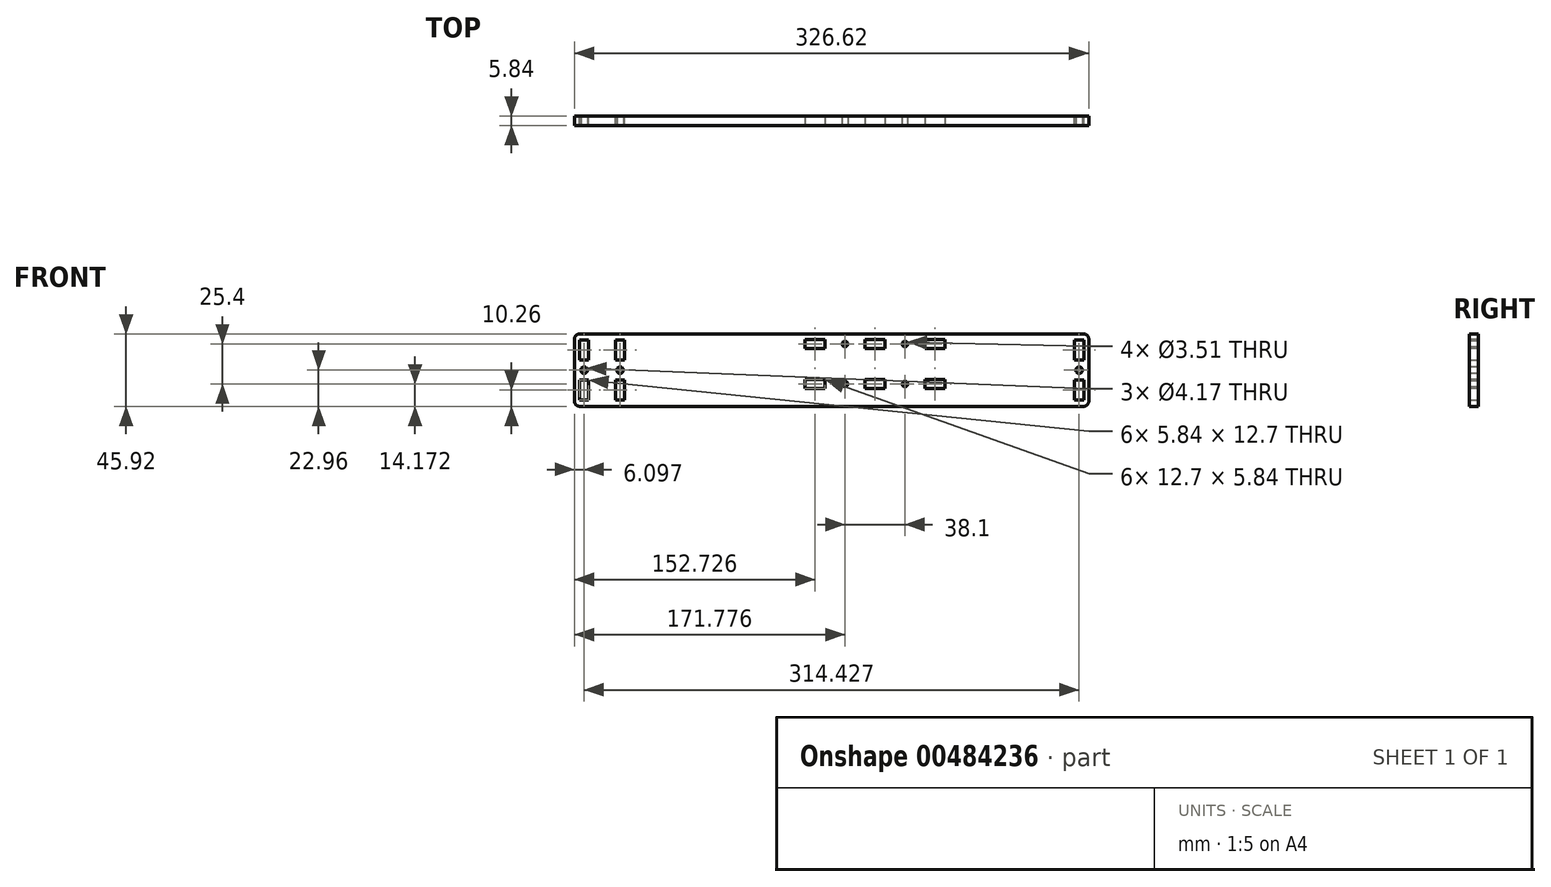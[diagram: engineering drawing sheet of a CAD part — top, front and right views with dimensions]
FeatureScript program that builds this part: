
annotation { "Feature Type Name" : "Feature", "Feature Type Description" : "" }
export const myFeature = defineFeature(function(context is Context, id is Id, definition is map)
    precondition{}
    {
        {
            var Q0;
            Q0=qCreatedBy(makeId("Front.planeOp"),FACE);
            var sketch = newSketch(context, id + "F0", { "sketchPlane" : qUnion([Q0])});
            skLineSegment(sketch, "E0.bottom", {"start": v(-163.3, 22.96) * mm, "end": v(163.3, 22.96) * mm});
            skLineSegment(sketch, "E0.top", {"start": v(-163.3, -22.96) * mm, "end": v(163.3, -22.96) * mm});
            skLineSegment(sketch, "E0.left", {"start": v(-163.3, 22.96) * mm, "end": v(-163.3, -22.96) * mm});
            skLineSegment(sketch, "E0.right", {"start": v(163.3, 22.96) * mm, "end": v(163.3, -22.96) * mm});
            skPoint(sketch, "E0.middle", {"position": v(0, 0) * mm});
            skLineSegment(sketch, "E1", {"start": v(-163.3, 0) * mm, "end": v(163.3, 0) * mm, "construction": true});
            skLineSegment(sketch, "E2.bottom", {"start": v(-160.13, 6.35) * mm, "end": v(-154.3, 6.35) * mm});
            skLineSegment(sketch, "E2.top", {"start": v(-160.13, 19.05) * mm, "end": v(-154.3, 19.05) * mm});
            skLineSegment(sketch, "E2.left", {"start": v(-160.13, 6.35) * mm, "end": v(-160.13, 19.05) * mm});
            skLineSegment(sketch, "E2.right", {"start": v(-154.3, 6.35) * mm, "end": v(-154.3, 19.05) * mm});
            skPoint(sketch, "E2.middle", {"position": v(-157.21, 12.7) * mm});
            skLineSegment(sketch, "E3.MirrorCS", {"start": v(-154.3, -6.35) * mm, "end": v(-154.3, -19.05) * mm});
            skLineSegment(sketch, "E4.MirrorCS", {"start": v(-160.13, -6.35) * mm, "end": v(-160.13, -19.05) * mm});
            skLineSegment(sketch, "E5.MirrorCS", {"start": v(-160.13, -19.05) * mm, "end": v(-154.3, -19.05) * mm});
            skLineSegment(sketch, "E6.MirrorCS", {"start": v(-160.13, -6.35) * mm, "end": v(-154.3, -6.35) * mm});
            skPoint(sketch, "E7.MirrorP", {"position": v(-157.21, -12.7) * mm});
            skLineSegment(sketch, "E8", {"start": v(-145.8, 22.96) * mm, "end": v(-145.8, -22.96) * mm, "construction": true});
            skPoint(sketch, "E9.MirrorP", {"position": v(-134.38, -12.7) * mm});
            skPoint(sketch, "E10.MirrorP", {"position": v(-134.38, 12.7) * mm});
            skLineSegment(sketch, "E11.MirrorCS", {"start": v(-131.46, -6.35) * mm, "end": v(-137.3, -6.35) * mm});
            skLineSegment(sketch, "E12.MirrorCS", {"start": v(-131.46, -19.05) * mm, "end": v(-137.3, -19.05) * mm});
            skLineSegment(sketch, "E13.MirrorCS", {"start": v(-131.46, -6.35) * mm, "end": v(-131.46, -19.05) * mm});
            skLineSegment(sketch, "E14.MirrorCS", {"start": v(-128.28, 0) * mm, "end": v(-454.9, 0) * mm, "construction": true});
            skLineSegment(sketch, "E15.MirrorCS", {"start": v(-137.3, -6.35) * mm, "end": v(-137.3, -19.05) * mm});
            skLineSegment(sketch, "E16.MirrorCS", {"start": v(-137.3, 6.35) * mm, "end": v(-137.3, 19.05) * mm});
            skLineSegment(sketch, "E17.MirrorCS", {"start": v(-131.46, 6.35) * mm, "end": v(-131.46, 19.05) * mm});
            skLineSegment(sketch, "E18.MirrorCS", {"start": v(-131.46, 19.05) * mm, "end": v(-137.3, 19.05) * mm});
            skLineSegment(sketch, "E19.MirrorCS", {"start": v(-131.46, 6.35) * mm, "end": v(-137.3, 6.35) * mm});
            skLineSegment(sketch, "E20", {"start": v(154.3, 22.96) * mm, "end": v(154.3, -22.96) * mm, "construction": true});
            skLineSegment(sketch, "E21.bottom", {"start": v(154.3, 19.05) * mm, "end": v(160.13, 19.05) * mm});
            skLineSegment(sketch, "E21.top", {"start": v(154.3, 6.35) * mm, "end": v(160.13, 6.35) * mm});
            skLineSegment(sketch, "E21.left", {"start": v(154.3, 19.05) * mm, "end": v(154.3, 6.35) * mm});
            skLineSegment(sketch, "E21.right", {"start": v(160.13, 19.05) * mm, "end": v(160.13, 6.35) * mm});
            skPoint(sketch, "E21.middle", {"position": v(157.21, 12.7) * mm});
            skLineSegment(sketch, "E22.MirrorCS", {"start": v(154.3, -19.05) * mm, "end": v(154.3, -6.35) * mm});
            skLineSegment(sketch, "E23.MirrorCS", {"start": v(154.3, -19.05) * mm, "end": v(160.13, -19.05) * mm});
            skPoint(sketch, "E24.MirrorP", {"position": v(157.21, -12.7) * mm});
            skLineSegment(sketch, "E25.MirrorCS", {"start": v(154.3, -6.35) * mm, "end": v(160.13, -6.35) * mm});
            skLineSegment(sketch, "E26.MirrorCS", {"start": v(160.13, -19.05) * mm, "end": v(160.13, -6.35) * mm});
            skSolve(sketch);
        }
        {
            var Q0;
            Q0 = qSketchRegion(id + "F0", true);
            extrude(context, id + "F1", {"entities" : qUnion([Q0]), "depth" : 5.84 * mm});
        }
        {
            var Q0;
            Q0=makeQuery(id+"F1.opExtrude","SWEPT_EDGE",EDGE,{"disambiguationData":[OSD([sQuery(id+"F0.wireOp",EDGE,"E0.bottom"),sQuery(id+"F0.wireOp",EDGE,"E0.left")])]});
            var Q1;
            Q1=makeQuery(id+"F1.opExtrude","SWEPT_EDGE",EDGE,{"disambiguationData":[OSD([sQuery(id+"F0.wireOp",EDGE,"E0.top"),sQuery(id+"F0.wireOp",EDGE,"E0.left")])]});
            var Q2;
            Q2=makeQuery(id+"F1.opExtrude","SWEPT_EDGE",EDGE,{"disambiguationData":[OSD([sQuery(id+"F0.wireOp",EDGE,"E0.bottom"),sQuery(id+"F0.wireOp",EDGE,"E0.right")])]});
            var Q3;
            Q3=makeQuery(id+"F1.opExtrude","SWEPT_EDGE",EDGE,{"disambiguationData":[OSD([sQuery(id+"F0.wireOp",EDGE,"E0.top"),sQuery(id+"F0.wireOp",EDGE,"E0.right")])]});
            fillet(context, id + "F2", {"entities" : qUnion([Q0, Q1, Q2, Q3]), "radius" : 3.17 * mm, "tangentPropagation" : true, "allowEdgeOverflow" : false});
        }
        {
            var Q0;
            Q0=makeQuery(id+"F1.opExtrude","CAP_FACE",FACE,{"disambiguationData":[OSD([sQuery(id+"F0.wireOp",EDGE,"E0.bottom"),sQuery(id+"F0.wireOp",EDGE,"E0.top"),sQuery(id+"F0.wireOp",EDGE,"E0.left"),sQuery(id+"F0.wireOp",EDGE,"E0.right"),sQuery(id+"F0.wireOp",EDGE,"E2.bottom"),sQuery(id+"F0.wireOp",EDGE,"E2.top"),sQuery(id+"F0.wireOp",EDGE,"E2.left"),sQuery(id+"F0.wireOp",EDGE,"E2.right"),sQuery(id+"F0.wireOp",EDGE,"E3.MirrorCS"),sQuery(id+"F0.wireOp",EDGE,"E4.MirrorCS"),sQuery(id+"F0.wireOp",EDGE,"E5.MirrorCS"),sQuery(id+"F0.wireOp",EDGE,"E6.MirrorCS"),sQuery(id+"F0.wireOp",EDGE,"E11.MirrorCS"),sQuery(id+"F0.wireOp",EDGE,"E12.MirrorCS"),sQuery(id+"F0.wireOp",EDGE,"E13.MirrorCS"),sQuery(id+"F0.wireOp",EDGE,"E15.MirrorCS"),sQuery(id+"F0.wireOp",EDGE,"E16.MirrorCS"),sQuery(id+"F0.wireOp",EDGE,"E17.MirrorCS"),sQuery(id+"F0.wireOp",EDGE,"E18.MirrorCS"),sQuery(id+"F0.wireOp",EDGE,"E19.MirrorCS"),sQuery(id+"F0.wireOp",EDGE,"E21.bottom"),sQuery(id+"F0.wireOp",EDGE,"E21.top"),sQuery(id+"F0.wireOp",EDGE,"E21.left"),sQuery(id+"F0.wireOp",EDGE,"E21.right"),sQuery(id+"F0.wireOp",EDGE,"E22.MirrorCS"),sQuery(id+"F0.wireOp",EDGE,"E23.MirrorCS"),sQuery(id+"F0.wireOp",EDGE,"E25.MirrorCS"),sQuery(id+"F0.wireOp",EDGE,"E26.MirrorCS")])],"isStart":false});
            var sketch = newSketch(context, id + "F3", { "sketchPlane" : qUnion([Q0])});
            skLineSegment(sketch, "E27", {"start": v(-157.21, 6.35) * mm, "end": v(-157.21, -6.35) * mm, "construction": true});
            skLineSegment(sketch, "E28", {"start": v(-134.38, -6.35) * mm, "end": v(-134.38, 6.35) * mm, "construction": true});
            skCircle(sketch, "E29", {"center": v(-134.38, 0) * mm, "radius": 2.08 * mm});
            skCircle(sketch, "E30", {"center": v(-157.21, 0) * mm, "radius": 2.08 * mm});
            skSolve(sketch);
        }
        {
            var Q0;
            Q0 = qSketchRegion(id + "F3", true);
            extrude(context, id + "F4", {"entities" : qUnion([Q0]), "operationType" : NewBodyOperationType.REMOVE, "oppositeDirection" : true, "depth" : 25.4 * mm});
        }
        {
            var Q0;
            Q0=makeQuery(id+"F1.opExtrude","CAP_FACE",FACE,{"disambiguationData":[OSD([sQuery(id+"F0.wireOp",EDGE,"E0.bottom"),sQuery(id+"F0.wireOp",EDGE,"E0.top"),sQuery(id+"F0.wireOp",EDGE,"E0.left"),sQuery(id+"F0.wireOp",EDGE,"E0.right"),sQuery(id+"F0.wireOp",EDGE,"E2.bottom"),sQuery(id+"F0.wireOp",EDGE,"E2.top"),sQuery(id+"F0.wireOp",EDGE,"E2.left"),sQuery(id+"F0.wireOp",EDGE,"E2.right"),sQuery(id+"F0.wireOp",EDGE,"E3.MirrorCS"),sQuery(id+"F0.wireOp",EDGE,"E4.MirrorCS"),sQuery(id+"F0.wireOp",EDGE,"E5.MirrorCS"),sQuery(id+"F0.wireOp",EDGE,"E6.MirrorCS"),sQuery(id+"F0.wireOp",EDGE,"E11.MirrorCS"),sQuery(id+"F0.wireOp",EDGE,"E12.MirrorCS"),sQuery(id+"F0.wireOp",EDGE,"E13.MirrorCS"),sQuery(id+"F0.wireOp",EDGE,"E15.MirrorCS"),sQuery(id+"F0.wireOp",EDGE,"E16.MirrorCS"),sQuery(id+"F0.wireOp",EDGE,"E17.MirrorCS"),sQuery(id+"F0.wireOp",EDGE,"E18.MirrorCS"),sQuery(id+"F0.wireOp",EDGE,"E19.MirrorCS"),sQuery(id+"F0.wireOp",EDGE,"E21.bottom"),sQuery(id+"F0.wireOp",EDGE,"E21.top"),sQuery(id+"F0.wireOp",EDGE,"E21.left"),sQuery(id+"F0.wireOp",EDGE,"E21.right"),sQuery(id+"F0.wireOp",EDGE,"E22.MirrorCS"),sQuery(id+"F0.wireOp",EDGE,"E23.MirrorCS"),sQuery(id+"F0.wireOp",EDGE,"E25.MirrorCS"),sQuery(id+"F0.wireOp",EDGE,"E26.MirrorCS")])],"isStart":false});
            var sketch = newSketch(context, id + "F5", { "sketchPlane" : qUnion([Q0])});
            skLineSegment(sketch, "E31", {"start": v(157.21, 6.35) * mm, "end": v(157.21, -6.35) * mm, "construction": true});
            skCircle(sketch, "E32", {"center": v(157.21, 0) * mm, "radius": 2.08 * mm});
            skSolve(sketch);
        }
        {
            var Q0;
            Q0 = qSketchRegion(id + "F5", true);
            extrude(context, id + "F6", {"entities" : qUnion([Q0]), "operationType" : NewBodyOperationType.REMOVE, "oppositeDirection" : true, "depth" : 25.4 * mm});
        }
        {
            var Q0;
            Q0=makeQuery(id+"F1.opExtrude","CAP_FACE",FACE,{"disambiguationData":[OSD([sQuery(id+"F0.wireOp",EDGE,"E0.bottom"),sQuery(id+"F0.wireOp",EDGE,"E0.top"),sQuery(id+"F0.wireOp",EDGE,"E0.left"),sQuery(id+"F0.wireOp",EDGE,"E0.right"),sQuery(id+"F0.wireOp",EDGE,"E2.bottom"),sQuery(id+"F0.wireOp",EDGE,"E2.top"),sQuery(id+"F0.wireOp",EDGE,"E2.left"),sQuery(id+"F0.wireOp",EDGE,"E2.right"),sQuery(id+"F0.wireOp",EDGE,"E3.MirrorCS"),sQuery(id+"F0.wireOp",EDGE,"E4.MirrorCS"),sQuery(id+"F0.wireOp",EDGE,"E5.MirrorCS"),sQuery(id+"F0.wireOp",EDGE,"E6.MirrorCS"),sQuery(id+"F0.wireOp",EDGE,"E11.MirrorCS"),sQuery(id+"F0.wireOp",EDGE,"E12.MirrorCS"),sQuery(id+"F0.wireOp",EDGE,"E13.MirrorCS"),sQuery(id+"F0.wireOp",EDGE,"E15.MirrorCS"),sQuery(id+"F0.wireOp",EDGE,"E16.MirrorCS"),sQuery(id+"F0.wireOp",EDGE,"E17.MirrorCS"),sQuery(id+"F0.wireOp",EDGE,"E18.MirrorCS"),sQuery(id+"F0.wireOp",EDGE,"E19.MirrorCS"),sQuery(id+"F0.wireOp",EDGE,"E21.bottom"),sQuery(id+"F0.wireOp",EDGE,"E21.top"),sQuery(id+"F0.wireOp",EDGE,"E21.left"),sQuery(id+"F0.wireOp",EDGE,"E21.right"),sQuery(id+"F0.wireOp",EDGE,"E22.MirrorCS"),sQuery(id+"F0.wireOp",EDGE,"E23.MirrorCS"),sQuery(id+"F0.wireOp",EDGE,"E25.MirrorCS"),sQuery(id+"F0.wireOp",EDGE,"E26.MirrorCS")])],"isStart":false});
            var sketch = newSketch(context, id + "F7", { "sketchPlane" : qUnion([Q0])});
            skLineSegment(sketch, "E33", {"start": v(-163.3, 16.61) * mm, "end": v(-4.23, 16.61) * mm, "construction": true});
            skLineSegment(sketch, "E34.bottom", {"start": v(-4.23, 19.53) * mm, "end": v(-16.93, 19.53) * mm});
            skLineSegment(sketch, "E34.top", {"start": v(-4.23, 13.7) * mm, "end": v(-16.93, 13.7) * mm});
            skLineSegment(sketch, "E34.left", {"start": v(-4.23, 19.53) * mm, "end": v(-4.23, 13.7) * mm});
            skLineSegment(sketch, "E34.right", {"start": v(-16.93, 19.53) * mm, "end": v(-16.93, 13.7) * mm});
            skPoint(sketch, "E34.middle", {"position": v(-10.58, 16.61) * mm});
            skLineSegment(sketch, "E35.1.0.0", {"start": v(21.17, 19.53) * mm, "end": v(21.17, 13.7) * mm});
            skLineSegment(sketch, "E35.1.0.1", {"start": v(33.87, 19.53) * mm, "end": v(33.87, 13.7) * mm});
            skLineSegment(sketch, "E35.1.0.2", {"start": v(33.87, 13.7) * mm, "end": v(21.17, 13.7) * mm});
            skPoint(sketch, "E35.1.0.3", {"position": v(27.52, 16.61) * mm});
            skLineSegment(sketch, "E35.1.0.4", {"start": v(33.87, 19.53) * mm, "end": v(21.17, 19.53) * mm});
            skLineSegment(sketch, "E35.2.0.0", {"start": v(59.27, 19.53) * mm, "end": v(59.27, 13.7) * mm});
            skLineSegment(sketch, "E35.2.0.1", {"start": v(71.97, 19.53) * mm, "end": v(71.97, 13.7) * mm});
            skLineSegment(sketch, "E35.2.0.2", {"start": v(71.97, 13.7) * mm, "end": v(59.27, 13.7) * mm});
            skPoint(sketch, "E35.2.0.3", {"position": v(65.62, 16.61) * mm});
            skLineSegment(sketch, "E35.2.0.4", {"start": v(71.97, 19.53) * mm, "end": v(59.27, 19.53) * mm});
            skLineSegment(sketch, "E35.direction1", {"start": v(-16.93, 13.7) * mm, "end": v(0, 13.7) * mm, "construction": true});
            skLineSegment(sketch, "E36", {"start": v(-4.23, 16.61) * mm, "end": v(21.17, 16.61) * mm, "construction": true});
            skCircle(sketch, "E37", {"center": v(8.47, 16.61) * mm, "radius": 1.75 * mm});
            skLineSegment(sketch, "E38", {"start": v(27.52, 19.53) * mm, "end": v(27.52, 13.7) * mm, "construction": true});
            skCircle(sketch, "E39.MirrorC", {"center": v(46.57, 16.61) * mm, "radius": 1.75 * mm});
            skLineSegment(sketch, "E40", {"start": v(0, 16.61) * mm, "end": v(0, -22.96) * mm, "construction": true});
            skLineSegment(sketch, "E41", {"start": v(0, -2.85) * mm, "end": v(20.16, -2.85) * mm, "construction": true});
            skLineSegment(sketch, "E42.bottom", {"start": v(-4.23, -5.87) * mm, "end": v(-16.93, -5.87) * mm});
            skLineSegment(sketch, "E42.top", {"start": v(-4.23, -11.7) * mm, "end": v(-16.93, -11.7) * mm});
            skLineSegment(sketch, "E42.left", {"start": v(-4.23, -5.87) * mm, "end": v(-4.23, -11.7) * mm});
            skLineSegment(sketch, "E42.right", {"start": v(-16.93, -5.87) * mm, "end": v(-16.93, -11.7) * mm});
            skPoint(sketch, "E42.middle", {"position": v(-10.58, -8.79) * mm});
            skLineSegment(sketch, "E43.1.0.0", {"start": v(33.87, -5.87) * mm, "end": v(33.87, -11.7) * mm});
            skLineSegment(sketch, "E43.1.0.1", {"start": v(33.87, -11.7) * mm, "end": v(21.17, -11.7) * mm});
            skPoint(sketch, "E43.1.0.2", {"position": v(27.52, -8.79) * mm});
            skLineSegment(sketch, "E43.1.0.3", {"start": v(33.87, -5.87) * mm, "end": v(21.17, -5.87) * mm});
            skLineSegment(sketch, "E43.1.0.4", {"start": v(21.17, -5.87) * mm, "end": v(21.17, -11.7) * mm});
            skLineSegment(sketch, "E43.2.0.0", {"start": v(71.97, -5.87) * mm, "end": v(71.97, -11.7) * mm});
            skLineSegment(sketch, "E43.2.0.1", {"start": v(71.97, -11.7) * mm, "end": v(59.27, -11.7) * mm});
            skPoint(sketch, "E43.2.0.2", {"position": v(65.62, -8.79) * mm});
            skLineSegment(sketch, "E43.2.0.3", {"start": v(71.97, -5.87) * mm, "end": v(59.27, -5.87) * mm});
            skLineSegment(sketch, "E43.2.0.4", {"start": v(59.27, -5.87) * mm, "end": v(59.27, -11.7) * mm});
            skLineSegment(sketch, "E43.direction1", {"start": v(-16.93, -11.7) * mm, "end": v(21.17, -11.7) * mm, "construction": true});
            skLineSegment(sketch, "E44", {"start": v(-4.23, -8.79) * mm, "end": v(21.17, -8.79) * mm, "construction": true});
            skCircle(sketch, "E45", {"center": v(8.47, -8.79) * mm, "radius": 1.75 * mm});
            skCircle(sketch, "E46.1.0.0", {"center": v(46.57, -8.79) * mm, "radius": 1.75 * mm});
            skLineSegment(sketch, "E46.direction1", {"start": v(8.47, -8.79) * mm, "end": v(46.57, -8.79) * mm, "construction": true});
            skLineSegment(sketch, "E47.trimOffspring", {"start": v(21.17, 16.61) * mm, "end": v(163.3, 16.61) * mm, "construction": true});
            skLineSegment(sketch, "E48.trimOffspring", {"start": v(6.71, 16.61) * mm, "end": v(10.22, 16.61) * mm, "construction": true});
            skSolve(sketch);
        }
        {
            var Q0;
            Q0 = qSketchRegion(id + "F7", true);
            extrude(context, id + "F8", {"entities" : qUnion([Q0]), "operationType" : NewBodyOperationType.REMOVE, "oppositeDirection" : true, "depth" : 25.4 * mm});
        }
    });
